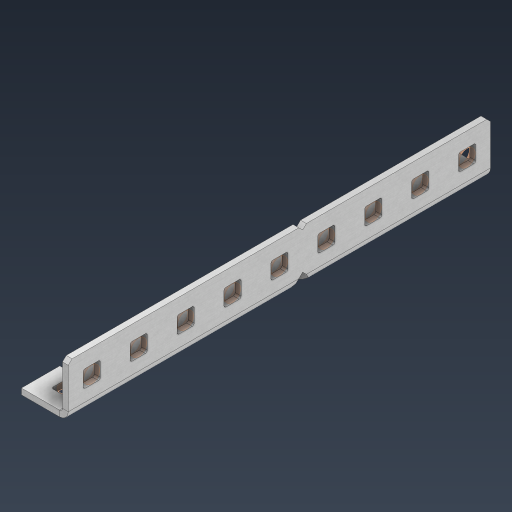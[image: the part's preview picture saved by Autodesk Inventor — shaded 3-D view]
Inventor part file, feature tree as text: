
AUTODESK INVENTOR PART (.ipt)
format: ipt  version: 2024.3 (Build 283343000, 343)  size: 570,368 bytes
history: native  units: in
note: dims shown in document units (in); Inventor stores cm internally (conversion verified against a paired STEP export)
features: other x34, extrude x25, sheet_metal_op x11, pattern_linear x2, mirror x1, chamfer x1, sketch x1
ambient origin geometry x8: Origin, YZ Plane, XZ Plane, XY Plane, X Axis, Y Axis, Z Axis, Center Point
bodies: Solid1 (feature_tree), Body (feature_tree)
feature tree (75):
  sheet_metal_op  "Flanges"
  other  "Flange Pattern Plane"
  other  "Flange Pattern Sketch"
  sheet_metal_op  "Flange Pattern"
  sheet_metal_op  "Body Pattern"
  pattern_linear  "Center Pattern"  Spacing1=4.5in  [1 undecoded]
  other  "Arc Length"
  mirror  "Notch Mirror"
  pattern_linear  "Notch Pattern"  Spacing1=0.0625in  [1 undecoded]
  chamfer  "End Chamfer"
  extrude  "Half Cut"  Depth=0.0625in
  other  "Plate1"
  sketch  "Sketch2"  dims[d0=1.0in d1=4.5in d2=0.0625in d3=0.0625in d4=0.0312in d5=0.125in d6=0.0625in d7=0.5in d8=90.0deg d9=0.0312in d10=0.25in d11=0.0625in d12=0.0625in d16=0.182in d17=0.02in d18=0.0625in d19=0.0in d20=0.25in d21=0.25in d38=3.5433in d40=0.5in d41=0.3937in d43=1.0in d46=0.172in d47=1.0in d48=0.0in d49=0.182in d50=0.02in d51=0.25in d52=0.25in d53=0.0625in d54=0.0in d55=0.172in d56=1.0in d57=0.0in d58=0.25in d60=3.5433in d62=0.5in d63=0.3937in d65=0.5in d85=0.1473in d86=0.1782in d88=0.04in d89=0.0625in d90=0.0in d91=0.04in d92=0.0491in d95=2.5in d96=0.04in d97=0.25in d98=45.0deg d99=0.25in d100=0.5in d101=0.0in d102=2.497in d106=0.182in d107=0.02in d108=0.5in d109=0.5in d110=0.0625in d111=0.0in d112=0.172in d113=0.5in d114=0.0in d117=0.5in d118=0.5in d119=0.5in]
  other  "Plate2"
  sheet_metal_op  "Bend1"
  sheet_metal_op  "Corner1"
  other  "Srf1"
  other  "Srf2"
  other  "Srf91"
  sheet_metal_op  "Body Pattern Sketch"
  other  "Srf92"
  other  "Srf786"
  other  "Srf823"
  other  "Srf824"
  other  "Srf825"
  other  "Srf826"
  other  "Srf827"
  other  "Srf828"
  other  "Srf829"
  other  "Srf856"
  other  "Srf857"
  other  "Srf858"
  other  "Srf859"
  other  "Srf860"
  other  "Srf861"
  other  "Srf862"
  other  "Srf889"
  other  "Srf890"
  other  "Srf891"
  other  "Srf892"
  other  "Srf893"
  other  "Srf894"
  other  "Srf895"
  other  "Srf896"
  sheet_metal_op  "Flange Stamp"
  sheet_metal_op  "Flange Circle"
  sheet_metal_op  "Body Stamp"
  sheet_metal_op  "Body Circle"
  other  "Center Stamp"
  other  "Center Circle"
  sheet_metal_op  "Notch"
  extrude  "ExtrusionSrf2"  Depth=0.0312in
  extrude  "ExtrusionSrf92"  Depth=0.5in
  extrude  "ExtrusionSrf823"  Depth=0.0625in
  extrude  "ExtrusionSrf824"  Depth=0.5in TaperAngle=90.0deg
  extrude  "ExtrusionSrf825"  Depth=0.5in
  extrude  "ExtrusionSrf826"  Depth=0.0625in
  extrude  "ExtrusionSrf827"  Depth=0.0625in
  extrude  "ExtrusionSrf828"  Depth=0.182in
  extrude  "ExtrusionSrf829"  Depth=0.02in
  extrude  "ExtrusionSrf856"  Depth=0.0625in
  extrude  "ExtrusionSrf857"  TaperAngle=0.0deg  [1 undecoded]
  extrude  "ExtrusionSrf858"  Depth=0.5in
  extrude  "ExtrusionSrf859"  Depth=0.5in
  extrude  "ExtrusionSrf860"  Depth=0.5in
  extrude  "ExtrusionSrf861"  Depth=0.5in
  extrude  "ExtrusionSrf862"  Depth=1.0in TaperAngle=0.0deg
  extrude  "ExtrusionSrf889"  Depth=0.182in
  extrude  "ExtrusionSrf890"  Depth=0.02in
  extrude  "ExtrusionSrf891"  Depth=0.5in
  extrude  "ExtrusionSrf892"  Depth=0.5in
  extrude  "ExtrusionSrf893"  Depth=0.0625in
  extrude  "ExtrusionSrf894"  TaperAngle=0.0deg  [1 undecoded]
  extrude  "ExtrusionSrf895"  Depth=0.5in
  extrude  "ExtrusionSrf896"  Depth=1.0in TaperAngle=0.0deg
note: 4 required parameter values undecoded (feature->parameter linkage not recoverable at this tier; creation-order binding heuristic only, values carry confidence <= 0.55)
